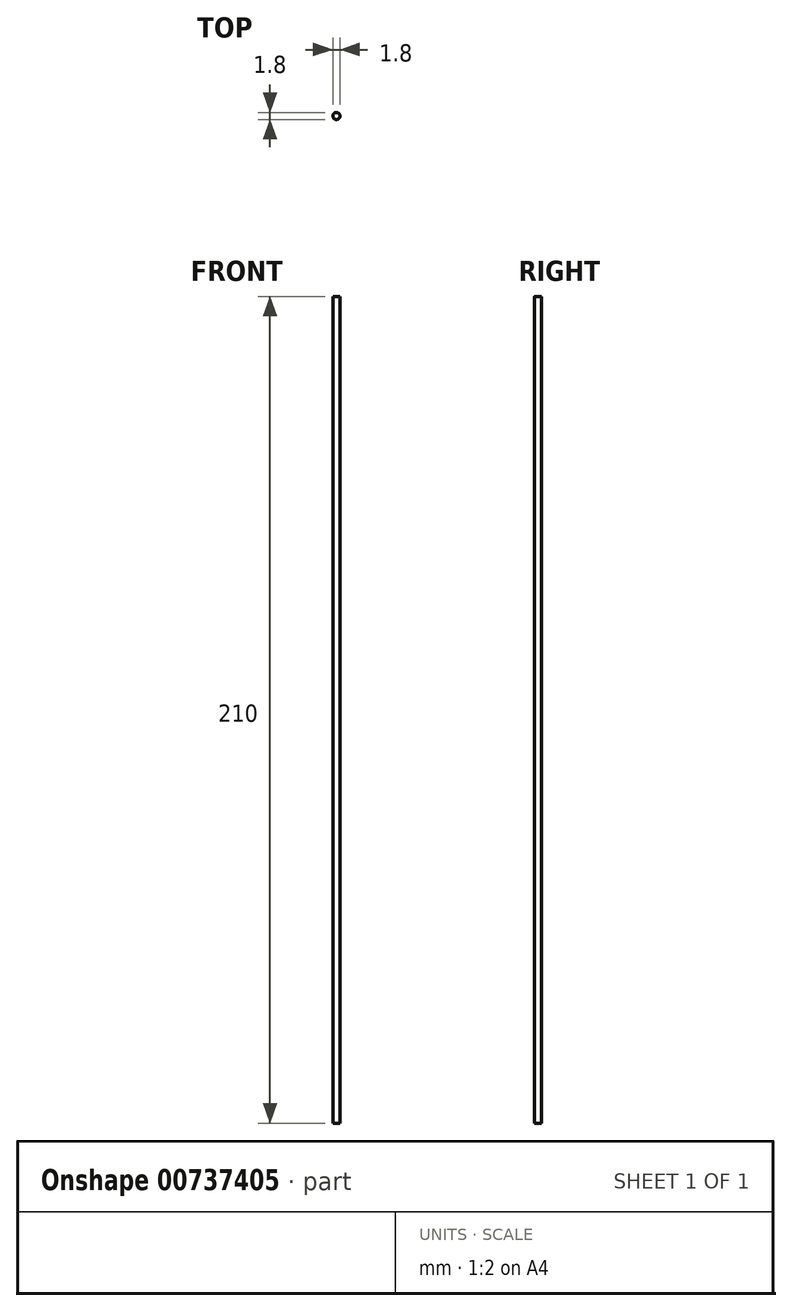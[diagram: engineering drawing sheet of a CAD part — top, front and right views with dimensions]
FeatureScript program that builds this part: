
annotation { "Feature Type Name" : "Feature", "Feature Type Description" : "" }
export const myFeature = defineFeature(function(context is Context, id is Id, definition is map)
    precondition{}
    {
        {
            var Q0;
            Q0=qCreatedBy(makeId("Top.planeOp"),FACE);
            var sketch = newSketch(context, id + "F0", { "sketchPlane" : qUnion([Q0])});
            skCircle(sketch, "E0", {"center": v(0, 0) * mm, "radius": 0.9 * mm});
            skSolve(sketch);
        }
        {
            var Q0;
            Q0 = qSketchRegion(id + "F0", true);
            extrude(context, id + "F1", {"entities" : qUnion([Q0]), "depth" : 210 * mm, "offsetDistance" : 25 * mm});
        }
    });
